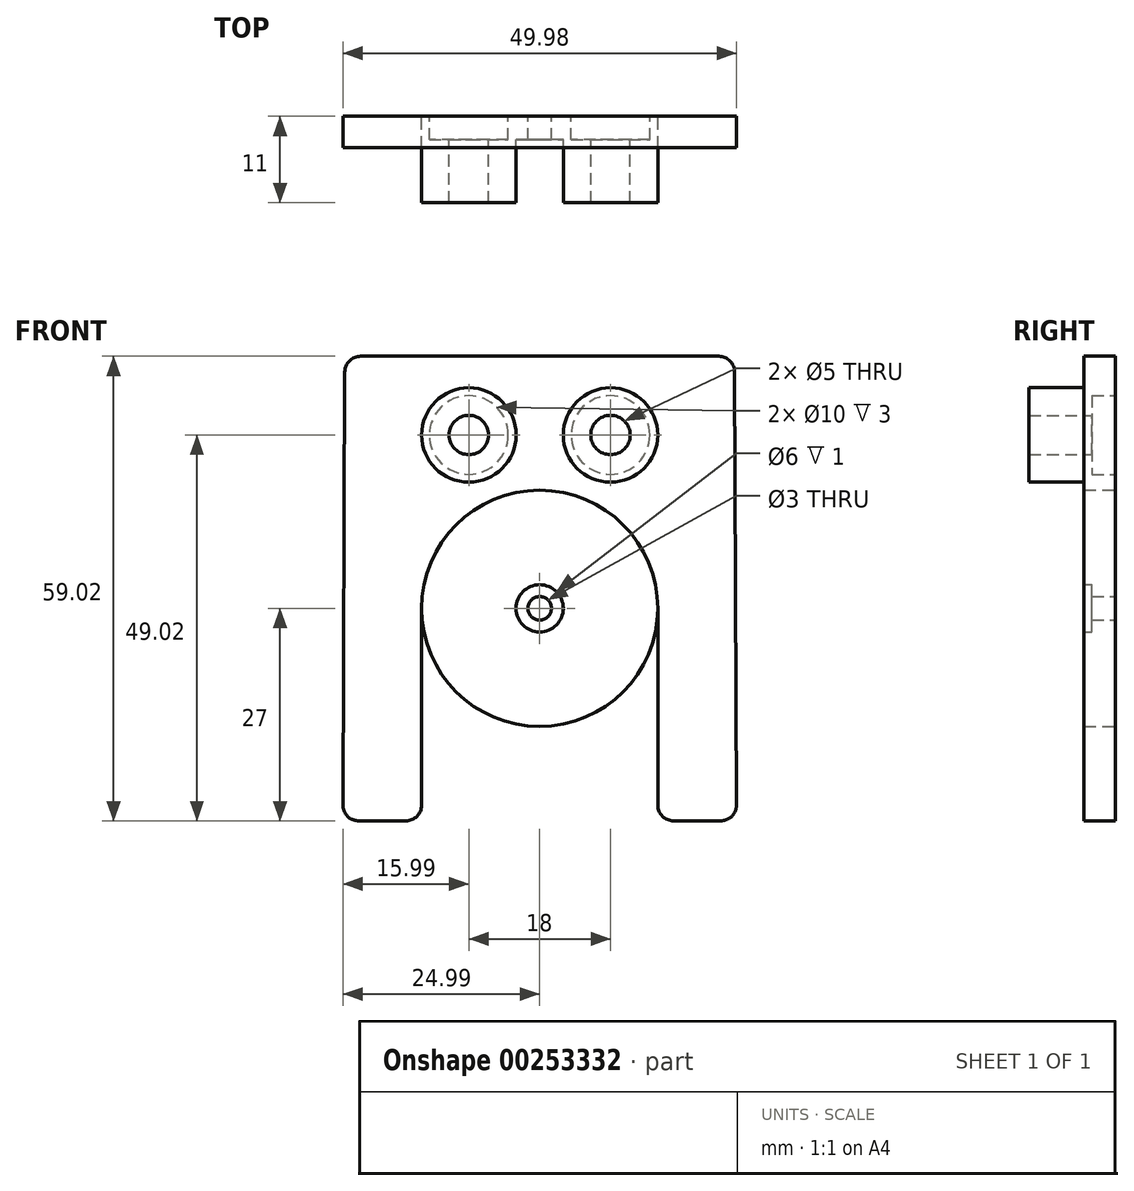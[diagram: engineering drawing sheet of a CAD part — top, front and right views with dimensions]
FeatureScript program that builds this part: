
annotation { "Feature Type Name" : "Feature", "Feature Type Description" : "" }
export const myFeature = defineFeature(function(context is Context, id is Id, definition is map)
    precondition{}
    {
        {
            var Q0;
            Q0=qCreatedBy(makeId("Front.planeOp"),FACE);
            var sketch = newSketch(context, id + "F0", { "sketchPlane" : qUnion([Q0])});
            skCircle(sketch, "E0", {"center": v(0, 0) * mm, "radius": 15 * mm});
            skCircle(sketch, "E1", {"center": v(0, 0) * mm, "radius": 1.5 * mm});
            skCircle(sketch, "E2", {"center": v(0, 0) * mm, "radius": 3 * mm});
            skSolve(sketch);
        }
        {
            var Q0;
            Q0=makeQuery(id+"F0.imprint","IMPRINT",FACE,{"disambiguationData":[TD([[makeQuery(id+"F0.imprint","IMPRINT",EDGE,{"derivedFrom":sQuery(id+"F0.wireOp",EDGE,"E0")}),1.0]])]});
            extrude(context, id + "F1", {"entities" : qUnion([Q0]), "depth" : 4 * mm});
        }
        {
            var Q0;
            Q0=qCreatedBy(makeId("Front.planeOp"),FACE);
            var sketch = newSketch(context, id + "F2", { "sketchPlane" : qUnion([Q0])});
            skArc(sketch, "E3.0.0", {"start": v(15, 0) * mm, "mid": v(0, 15) * mm, "end": v(-15, 0) * mm});
            skLineSegment(sketch, "E4.1", {"start": v(-22.76, 32.02) * mm, "end": v(0, 32.02) * mm});
            skPoint(sketch, "E5.visualSharp", {"position": v(-25, -27) * mm});
            skPoint(sketch, "E6.visualSharp", {"position": v(-15, -27) * mm});
            skPoint(sketch, "E7.visualSharp", {"position": v(-24.75, 32.02) * mm});
            skArc(sketch, "E7.filletArc", {"start": v(-22.76, 32.02) * mm, "mid": v(-24.17, 31.44) * mm, "end": v(-24.76, 30.03) * mm});
            skLineSegment(sketch, "E8", {"start": v(-24.76, 30.03) * mm, "end": v(-25, -24.99) * mm});
            skLineSegment(sketch, "E9", {"start": v(-15, 0) * mm, "end": v(-15, -25) * mm});
            skLineSegment(sketch, "E10", {"start": v(-23, -27) * mm, "end": v(-17, -27) * mm});
            skPoint(sketch, "E11", {"position": v(0, 32.02) * mm});
            skArc(sketch, "E12.MirrorCS", {"start": v(22.76, 32.02) * mm, "mid": v(24.17, 31.44) * mm, "end": v(24.76, 30.03) * mm});
            skPoint(sketch, "E13.MirrorP", {"position": v(15, -27) * mm});
            skLineSegment(sketch, "E14.MirrorCS", {"start": v(23, -27) * mm, "end": v(17, -27) * mm});
            skPoint(sketch, "E15.MirrorP", {"position": v(24.75, 32.02) * mm});
            skLineSegment(sketch, "E16.MirrorCS", {"start": v(24.76, 30.03) * mm, "end": v(25, -24.99) * mm});
            skLineSegment(sketch, "E17.MirrorCS", {"start": v(15, 0) * mm, "end": v(15, -25) * mm});
            skLineSegment(sketch, "E18.MirrorCS", {"start": v(22.76, 32.02) * mm, "end": v(0, 32.02) * mm});
            skPoint(sketch, "E19.MirrorP", {"position": v(25, -27) * mm});
            skArc(sketch, "E20.filletArc", {"start": v(-25, -24.99) * mm, "mid": v(-24.4, -26.4) * mm, "end": v(-23, -27) * mm});
            skArc(sketch, "E21.filletArc", {"start": v(-17, -27) * mm, "mid": v(-15.59, -26.41) * mm, "end": v(-15, -25) * mm});
            skArc(sketch, "E22.filletArc", {"start": v(15, -25) * mm, "mid": v(15.59, -26.41) * mm, "end": v(17, -27) * mm});
            skArc(sketch, "E23.filletArc", {"start": v(23, -27) * mm, "mid": v(24.4, -26.4) * mm, "end": v(25, -24.99) * mm});
            skSolve(sketch);
        }
        {
            var Q0;
            Q0=makeQuery(id+"F0.imprint","IMPRINT",FACE,{"disambiguationData":[TD([[makeQuery(id+"F0.imprint","IMPRINT",EDGE,{"derivedFrom":sQuery(id+"F0.wireOp",EDGE,"E1")}),-1.0]])]});
            extrude(context, id + "F3", {"entities" : qUnion([Q0]), "operationType" : NewBodyOperationType.ADD, "depth" : 3 * mm});
        }
        {
            var Q0;
            Q0=makeQuery(id+"F2.imprint","IMPRINT",FACE,{"disambiguationData":[TD([[makeQuery(id+"F2.imprint","IMPRINT",EDGE,{"derivedFrom":sQuery(id+"F2.wireOp",EDGE,"E3.0.0")}),-1.0]])]});
            extrude(context, id + "F4", {"entities" : qUnion([Q0]), "depth" : 4 * mm});
        }
        {
            var Q0;
            Q0=makeQuery(id+"F4.opExtrude","CAP_FACE",FACE,{"disambiguationData":[OSD([sQuery(id+"F2.wireOp",EDGE,"E3.0.0"),sQuery(id+"F2.wireOp",EDGE,"Nwsv7krC-Ntaf-TlhP-NB04-7WwulJXKLoHk.left"),sQuery(id+"F2.wireOp",EDGE,"E4.1"),sQuery(id+"F2.wireOp",EDGE,"W9fuY7bi-bEnq-6AFt-82Ec-zvvuWODFFQIf"),sQuery(id+"F2.wireOp",EDGE,"CAd3NbRl-uGJZ-k2Xo-gCQ1-bfxUW1wcl8y6"),sQuery(id+"F2.wireOp",EDGE,"7a9eb101-d4b5-4dd8-8326-b3acec89c4cb.filletArc"),sQuery(id+"F2.wireOp",EDGE,"ad46ea01-597d-4297-9f66-1d08d4899aa0.filletArc"),sQuery(id+"F2.wireOp",EDGE,"ImvzVIdQ-Umz6-QFDg-ckjz-w6vPKLBXCNsW"),sQuery(id+"F2.wireOp",EDGE,"YkzlAQjH-skRa-YgoC-N0Ey-kTPx22tdUU4O"),sQuery(id+"F2.wireOp",EDGE,"Mc3YCZKi-kUl7-mPYj-OtbN-YDg1YAh75A58"),sQuery(id+"F2.wireOp",EDGE,"E5.filletArc"),sQuery(id+"F2.wireOp",EDGE,"e3519a6b-dbf4-42c3-a287-dca184a5bc19.filletArc"),sQuery(id+"F2.wireOp",EDGE,"584f88d5-4728-4428-8665-bc3ae63d1e32.filletArc"),sQuery(id+"F2.wireOp",EDGE,"E6.filletArc")])],"isStart":false});
            var sketch = newSketch(context, id + "F5", { "sketchPlane" : qUnion([Q0])});
            skCircle(sketch, "E24", {"center": v(-9, 22.02) * mm, "radius": 5 * mm});
            skCircle(sketch, "E25", {"center": v(-9, 22.02) * mm, "radius": 2.5 * mm});
            skCircle(sketch, "E26", {"center": v(9, 22.02) * mm, "radius": 5 * mm});
            skCircle(sketch, "E27", {"center": v(9, 22.02) * mm, "radius": 2.5 * mm});
            skCircle(sketch, "E28", {"center": v(-9, 22.02) * mm, "radius": 6 * mm});
            skCircle(sketch, "E29", {"center": v(9, 22.02) * mm, "radius": 6 * mm});
            skLineSegment(sketch, "E30", {"start": v(0, 0) * mm, "end": v(0, 32.02) * mm, "construction": true});
            skLineSegment(sketch, "E31", {"start": v(9, 22.02) * mm, "end": v(-9, 22.02) * mm, "construction": true});
            skPoint(sketch, "E32", {"position": v(0, 22.02) * mm});
            skSolve(sketch);
        }
        {
            var Q0;
            Q0=makeQuery(id+"F5.imprint","IMPRINT",FACE,{"disambiguationData":[TD([[makeQuery(id+"F5.imprint","IMPRINT",EDGE,{"derivedFrom":sQuery(id+"F5.wireOp",EDGE,"E26")}),-1.0]])]});
            var Q1;
            Q1=makeQuery(id+"F5.imprint","IMPRINT",FACE,{"disambiguationData":[TD([[makeQuery(id+"F5.imprint","IMPRINT",EDGE,{"derivedFrom":sQuery(id+"F5.wireOp",EDGE,"E24")}),-1.0]])]});
            extrude(context, id + "F6", {"entities" : qUnion([Q0, Q1]), "operationType" : NewBodyOperationType.ADD, "depth" : 7 * mm});
        }
        {
            var Q0;
            Q0=makeQuery(id+"F5.imprint","IMPRINT",FACE,{"disambiguationData":[TD([[makeQuery(id+"F5.imprint","IMPRINT",EDGE,{"derivedFrom":sQuery(id+"F5.wireOp",EDGE,"E26")}),1.0]])]});
            var Q1;
            Q1=makeQuery(id+"F5.imprint","IMPRINT",FACE,{"disambiguationData":[TD([[makeQuery(id+"F5.imprint","IMPRINT",EDGE,{"derivedFrom":sQuery(id+"F5.wireOp",EDGE,"E24")}),1.0]])]});
            extrude(context, id + "F7", {"entities" : qUnion([Q0, Q1]), "operationType" : NewBodyOperationType.ADD, "depth" : 7 * mm});
        }
        {
            var Q0;
            Q0=makeQuery(id+"F6.boolean.opBoolean","SPLIT",FACE,{"disambiguationData":[TD([makeQuery(id+"F6.opExtrude","SWEPT_FACE",FACE,{"disambiguationData":[OSD([sQuery(id+"F5.wireOp",EDGE,"E26")])]})])],"derivedFrom":makeQuery(id+"F4.opExtrude","CAP_FACE",FACE,{"disambiguationData":[OSD([sQuery(id+"F2.wireOp",EDGE,"E3.0.0"),sQuery(id+"F2.wireOp",EDGE,"Nwsv7krC-Ntaf-TlhP-NB04-7WwulJXKLoHk.left"),sQuery(id+"F2.wireOp",EDGE,"E4.1"),sQuery(id+"F2.wireOp",EDGE,"W9fuY7bi-bEnq-6AFt-82Ec-zvvuWODFFQIf"),sQuery(id+"F2.wireOp",EDGE,"CAd3NbRl-uGJZ-k2Xo-gCQ1-bfxUW1wcl8y6"),sQuery(id+"F2.wireOp",EDGE,"7a9eb101-d4b5-4dd8-8326-b3acec89c4cb.filletArc"),sQuery(id+"F2.wireOp",EDGE,"ad46ea01-597d-4297-9f66-1d08d4899aa0.filletArc"),sQuery(id+"F2.wireOp",EDGE,"ImvzVIdQ-Umz6-QFDg-ckjz-w6vPKLBXCNsW"),sQuery(id+"F2.wireOp",EDGE,"YkzlAQjH-skRa-YgoC-N0Ey-kTPx22tdUU4O"),sQuery(id+"F2.wireOp",EDGE,"Mc3YCZKi-kUl7-mPYj-OtbN-YDg1YAh75A58"),sQuery(id+"F2.wireOp",EDGE,"E5.filletArc"),sQuery(id+"F2.wireOp",EDGE,"e3519a6b-dbf4-42c3-a287-dca184a5bc19.filletArc"),sQuery(id+"F2.wireOp",EDGE,"584f88d5-4728-4428-8665-bc3ae63d1e32.filletArc"),sQuery(id+"F2.wireOp",EDGE,"E6.filletArc")])],"isStart":false})});
            var Q1;
            Q1=makeQuery(id+"F6.boolean.opBoolean","SPLIT",FACE,{"disambiguationData":[TD([makeQuery(id+"F6.opExtrude","SWEPT_FACE",FACE,{"disambiguationData":[OSD([sQuery(id+"F5.wireOp",EDGE,"E24")])]})])],"derivedFrom":makeQuery(id+"F4.opExtrude","CAP_FACE",FACE,{"disambiguationData":[OSD([sQuery(id+"F2.wireOp",EDGE,"E3.0.0"),sQuery(id+"F2.wireOp",EDGE,"Nwsv7krC-Ntaf-TlhP-NB04-7WwulJXKLoHk.left"),sQuery(id+"F2.wireOp",EDGE,"E4.1"),sQuery(id+"F2.wireOp",EDGE,"W9fuY7bi-bEnq-6AFt-82Ec-zvvuWODFFQIf"),sQuery(id+"F2.wireOp",EDGE,"CAd3NbRl-uGJZ-k2Xo-gCQ1-bfxUW1wcl8y6"),sQuery(id+"F2.wireOp",EDGE,"7a9eb101-d4b5-4dd8-8326-b3acec89c4cb.filletArc"),sQuery(id+"F2.wireOp",EDGE,"ad46ea01-597d-4297-9f66-1d08d4899aa0.filletArc"),sQuery(id+"F2.wireOp",EDGE,"ImvzVIdQ-Umz6-QFDg-ckjz-w6vPKLBXCNsW"),sQuery(id+"F2.wireOp",EDGE,"YkzlAQjH-skRa-YgoC-N0Ey-kTPx22tdUU4O"),sQuery(id+"F2.wireOp",EDGE,"Mc3YCZKi-kUl7-mPYj-OtbN-YDg1YAh75A58"),sQuery(id+"F2.wireOp",EDGE,"E5.filletArc"),sQuery(id+"F2.wireOp",EDGE,"e3519a6b-dbf4-42c3-a287-dca184a5bc19.filletArc"),sQuery(id+"F2.wireOp",EDGE,"584f88d5-4728-4428-8665-bc3ae63d1e32.filletArc"),sQuery(id+"F2.wireOp",EDGE,"E6.filletArc")])],"isStart":false})});
            extrude(context, id + "F8", {"entities" : qUnion([Q0, Q1]), "operationType" : NewBodyOperationType.REMOVE, "endBound" : BoundingType.THROUGH_ALL, "oppositeDirection" : true, "depth" : 25 * mm});
        }
        {
            var Q0;
            Q0=makeQuery(id+"F4.opExtrude","CAP_FACE",FACE,{"disambiguationData":[OSD([sQuery(id+"F2.wireOp",EDGE,"E3.0.0"),sQuery(id+"F2.wireOp",EDGE,"E4.1"),sQuery(id+"F2.wireOp",EDGE,"E7.filletArc"),sQuery(id+"F2.wireOp",EDGE,"E8"),sQuery(id+"F2.wireOp",EDGE,"E9"),sQuery(id+"F2.wireOp",EDGE,"E10"),sQuery(id+"F2.wireOp",EDGE,"E12.MirrorCS"),sQuery(id+"F2.wireOp",EDGE,"E14.MirrorCS"),sQuery(id+"F2.wireOp",EDGE,"E16.MirrorCS"),sQuery(id+"F2.wireOp",EDGE,"E17.MirrorCS"),sQuery(id+"F2.wireOp",EDGE,"E18.MirrorCS"),sQuery(id+"F2.wireOp",EDGE,"E20.filletArc"),sQuery(id+"F2.wireOp",EDGE,"E21.filletArc"),sQuery(id+"F2.wireOp",EDGE,"E22.filletArc"),sQuery(id+"F2.wireOp",EDGE,"E23.filletArc")])],"isStart":true});
            var sketch = newSketch(context, id + "F9", { "sketchPlane" : qUnion([Q0])});
            skCircle(sketch, "E33", {"center": v(-9, 22.02) * mm, "radius": 5 * mm});
            skCircle(sketch, "E34", {"center": v(9, 22.02) * mm, "radius": 5 * mm});
            skSolve(sketch);
        }
        {
            var Q0;
            Q0=makeQuery(id+"F9.imprint","IMPRINT",FACE,{"disambiguationData":[TD([[makeQuery(id+"F9.imprint","IMPRINT",EDGE,{"derivedFrom":sQuery(id+"F9.wireOp",EDGE,"E33")}),1.0]])]});
            var Q1;
            Q1=makeQuery(id+"F9.imprint","IMPRINT",FACE,{"disambiguationData":[TD([[makeQuery(id+"F9.imprint","IMPRINT",EDGE,{"derivedFrom":sQuery(id+"F9.wireOp",EDGE,"E34")}),1.0]])]});
            extrude(context, id + "F10", {"entities" : qUnion([Q0, Q1]), "operationType" : NewBodyOperationType.REMOVE, "oppositeDirection" : true, "depth" : 3 * mm});
        }
    });
